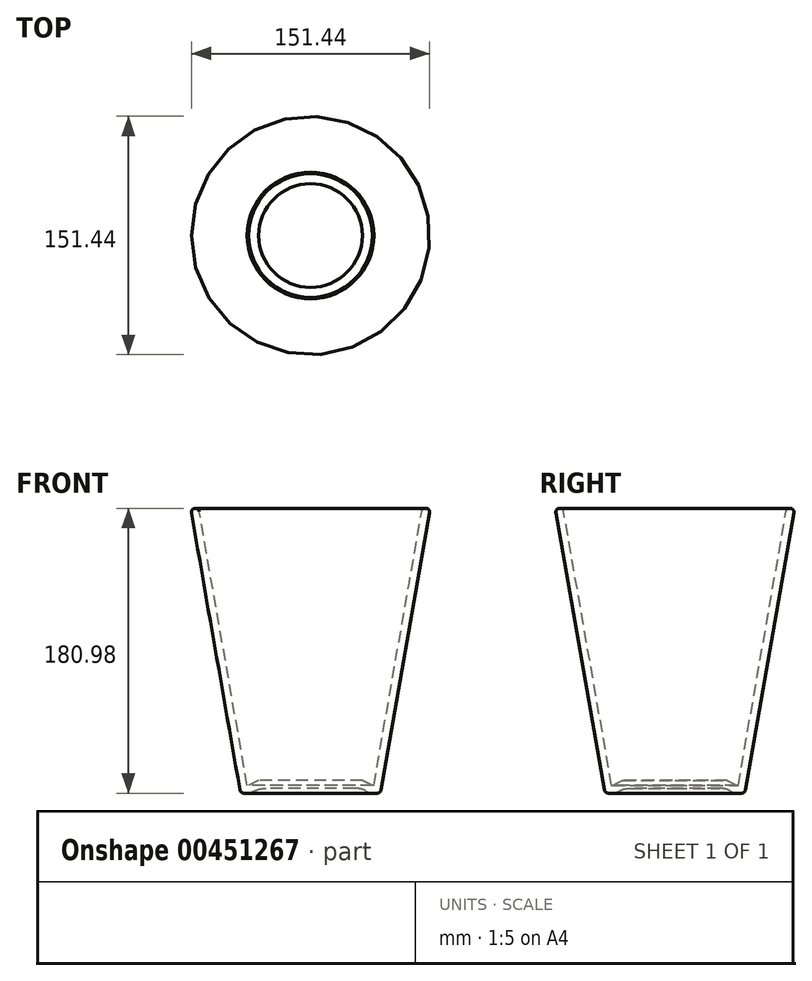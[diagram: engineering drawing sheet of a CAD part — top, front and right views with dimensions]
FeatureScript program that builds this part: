
annotation { "Feature Type Name" : "Feature", "Feature Type Description" : "" }
export const myFeature = defineFeature(function(context is Context, id is Id, definition is map)
    precondition{}
    {
        {
            var Q0;
            Q0=qCreatedBy(makeId("Front.planeOp"),FACE);
            var sketch = newSketch(context, id + "F0", { "sketchPlane" : qUnion([Q0])});
            skLineSegment(sketch, "E0", {"start": v(0, 3.18) * mm, "end": v(-31.75, 3.18) * mm});
            skLineSegment(sketch, "E1", {"start": v(-31.75, 3.17) * mm, "end": v(-38.1, 0) * mm});
            skLineSegment(sketch, "E2", {"start": v(-38.1, 0) * mm, "end": v(-44.45, 0) * mm});
            skLineSegment(sketch, "E3", {"start": v(-44.45, 0) * mm, "end": v(-76.2, 180.98) * mm});
            skLineSegment(sketch, "E4", {"start": v(-76.2, 180.97) * mm, "end": v(0, 180.97) * mm});
            skLineSegment(sketch, "E5", {"start": v(0, 180.97) * mm, "end": v(0, 3.18) * mm});
            skSolve(sketch);
        }
        {
            var Q0;
            Q0=makeQuery(id+"F0.imprint","IMPRINT",FACE,{"disambiguationData":[TD([[makeQuery(id+"F0.imprint","IMPRINT",EDGE,{"derivedFrom":sQuery(id+"F0.wireOp",EDGE,"E0")}),-1.0]])]});
            var Q1;
            Q1=sQuery(id+"F0.wireOp",EDGE,"E5");
            revolve(context, id + "F1", {"entities" : qUnion([Q0]), "axis" : qUnion([Q1]), "revolveType" : RevolveType.FULL});
        }
        {
            var Q0;
            Q0=makeQuery(id+"F1.opRevolve","SWEPT_FACE",FACE,{"disambiguationData":[OSD([sQuery(id+"F0.wireOp",EDGE,"E4")])]});
            shell(context, id + "F2", {"entities" : qUnion([Q0]), "thickness" : 5.08 * mm});
        }
        {
            var Q0;
            Q0=makeQuery(id+"F1.opRevolve","SWEPT_EDGE",EDGE,{"disambiguationData":[OSD([sQuery(id+"F0.wireOp",EDGE,"E3"),sQuery(id+"F0.wireOp",EDGE,"E4")])]});
            var Q1;
            Q1=makeQuery(id+"F2.opShell","OFFSET_EDGE",EDGE,{"disambiguationData":[OSD([sQuery(id+"F0.wireOp",EDGE,"E3"),sQuery(id+"F0.wireOp",EDGE,"E4")])]});
            fillet(context, id + "F3", {"entities" : qUnion([Q0, Q1]), "radius" : 2.54 * mm, "tangentPropagation" : true, "allowEdgeOverflow" : false});
        }
        {
            var Q0;
            Q0=makeQuery(id+"F1.opRevolve","SWEPT_EDGE",EDGE,{"disambiguationData":[OSD([sQuery(id+"F0.wireOp",EDGE,"E2"),sQuery(id+"F0.wireOp",EDGE,"E3")])]});
            var Q1;
            Q1=makeQuery(id+"F1.opRevolve","SWEPT_EDGE",EDGE,{"disambiguationData":[OSD([sQuery(id+"F0.wireOp",EDGE,"E1"),sQuery(id+"F0.wireOp",EDGE,"E2")])]});
            fillet(context, id + "F4", {"entities" : qUnion([Q0, Q1]), "radius" : 2.54 * mm, "tangentPropagation" : true, "allowEdgeOverflow" : false});
        }
        {
            var Q0;
            Q0=makeQuery(id+"F1.opRevolve","SWEPT_EDGE",EDGE,{"disambiguationData":[OSD([sQuery(id+"F0.wireOp",EDGE,"E0"),sQuery(id+"F0.wireOp",EDGE,"E1")])]});
            fillet(context, id + "F5", {"entities" : qUnion([Q0]), "radius" : 15.24 * mm, "tangentPropagation" : true, "allowEdgeOverflow" : false});
        }
    });
